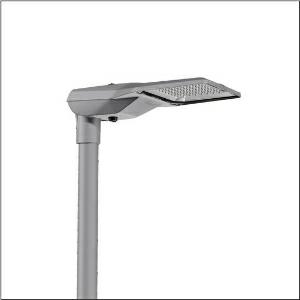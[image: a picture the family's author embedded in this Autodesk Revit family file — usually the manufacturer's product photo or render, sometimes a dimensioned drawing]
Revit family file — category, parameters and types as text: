
# Revit family: streetlight_sl_21_midi___st1_0a_5xe3d33t08mb_6958
name_source: partatom
category: Lighting Fixtures
units: mm (PartAtom-declared; Revit-internal decimal feet)

## family parameters
Cut with Voids When Loaded = No
Host = Face
Light Source = No
Part Type = Normal
Room Calculation Point = No
Round Connector Dimension = Use Diameter
Shared = No

## types (1)
- --- (1 x LED, 18270 lm, 136 W, 3000K)
    Apparent Load = 136 VA
    CIE Flux Codes = 37 72 97 100 100
    Color Rendering = 70
    Color Temperature = 3000K
    Default Elevation = 1800 mm
    Description = Streetlight SL 21 midi, mast luminaire, primary light control with lens, of PMMA, primary optical cover: cover, of toughened safety glass, transparent, light distribution: ST1.0a, light emission: direct distribution, primary light characteristic: asymmetric, installation type: side-entry, post-top, LED, High Power LED, rated luminous flux: 18.270lm, luminous efficacy: 134lm/W, light colour: 730, colour temperature: 3000K, control gear: D4i, control: flexible luminous flux parameterisation, time-dependent luminous flux control, constant luminous flux control, overheat protection, pre-setting: logarithmic dimming characteristic, mains connection: 230..240V, AC, 50/60Hz, start of lifetime: 136W, end of service life: 142W, reduction: 61W, luminaire housing, of diecast aluminium, powder-coated, SITECO metallic grey (DB 702S), corrosivity category C5 high according to DIN EN ISO 12944, please order mast flange separately, inclination adjustable: 0°, 5°, 10°, 15°, sealing non-destructively replaceable, multi-level sealing system, length: 644mm, width: 335mm, height: 110mm, mast flange for spigot size: 42mm (side-entry): 5XC10008XM4, 60/48mm (side-entry/post-top): 5XC10108XM2, 76/60mm (side-entry/post-top): 5XC10108XM1, mounting height: 4..8m, Smart Interface below and above, protection rating (complete): IP66, insulation class (complete): insulation class II (safety insulation), certification: CE, ENEC, ENEC+, VDE, impact resistance: IK10, permissible operating ambient temperature for outdoor applications: -40..+50°C, standard-compliant lighting for roads and squares, packaging unit: 1 piece

Light Distribution: ST1.0a
    Height = 111 mm
    Lamp = 1 x LED
    Lamp Light Flux = 18270 lm
    Lamp Power = 136 W
    Lamp count = 1
    Length = 644 mm
    Luminous efficacy = 134 lm/W
    Manufacturer = Siteco
    ModVariant = No
    Model = 5XE3D33T08MB
    Number of Poles = 1
    OnlyDefault = Yes
    Power Factor = 1
    Product Name = Streetlight SL 21 midi | ST1.0a
    Product group = mast luminaire | pylon top
    ProductGroupID = 6100
    Protection Class = Protection class II
    Protection Degree = IP 66
    RLX_Detail_Level = 1
    RLX_Emergency_Light_Flux = 0 lm
    RLX_Emergency_Type = 0
    RLX_Emergency_Type_DB = No
    RlxData = <blob elided: 26941 chars, md5=c0af792f>
    Socket = socket
    Standby Power = 0 W
    System Light Flux = 18270 lm
    System Power = 136 W
    Type Comments = factory setting: luminous flux: 100 % | dim-lin: 254 | 695 mA
    Type Image = l_1004304.jpg
    URL = http://relux.com
    VarID = @adj_186731
    Voltage = 0 V
    Weight = 0.00 kg
    Width = 336 mm

## geometry (parser evidence)
native form markers: Blend x4, Sweep x13
no freeform markers — native parametric forms only
